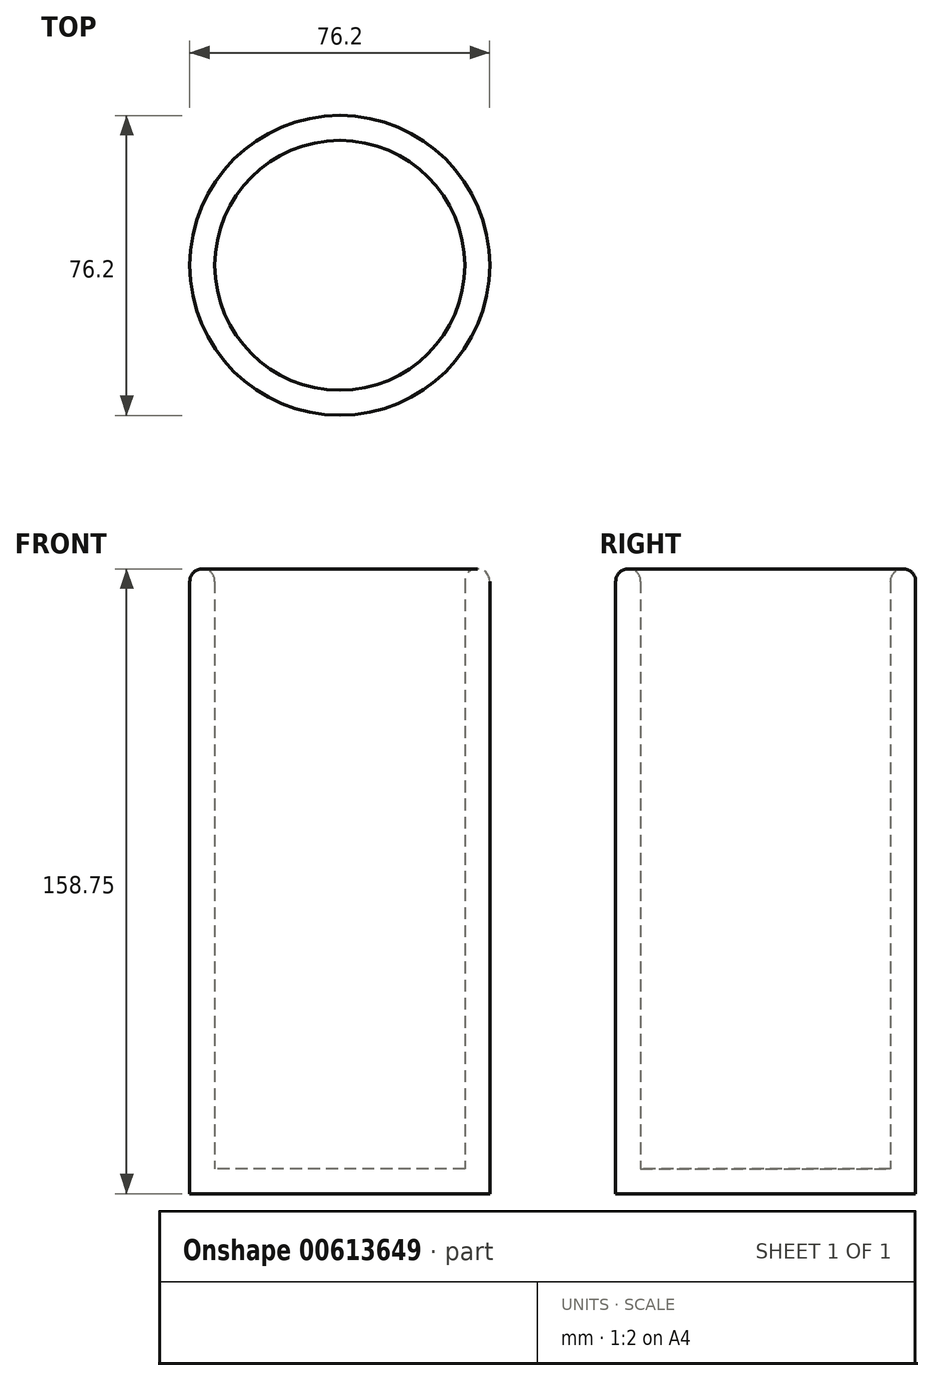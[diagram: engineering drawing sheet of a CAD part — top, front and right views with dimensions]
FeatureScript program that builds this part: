
annotation { "Feature Type Name" : "Feature", "Feature Type Description" : "" }
export const myFeature = defineFeature(function(context is Context, id is Id, definition is map)
    precondition{}
    {
        {
            var Q0;
            Q0=qCreatedBy(makeId("Top.planeOp"),FACE);
            var sketch = newSketch(context, id + "F0", { "sketchPlane" : qUnion([Q0])});
            skCircle(sketch, "E0", {"center": v(-62.36, 26.82) * mm, "radius": 38.1 * mm});
            skSolve(sketch);
        }
        {
            var Q0;
            Q0=makeQuery(id+"F0.imprint","IMPRINT",FACE,{"disambiguationData":[TD([[makeQuery(id+"F0.imprint","IMPRINT",EDGE,{"derivedFrom":sQuery(id+"F0.wireOp",EDGE,"E0")}),1.0]])]});
            extrude(context, id + "F1", {"entities" : qUnion([Q0]), "depth" : 6.35 * mm, "offsetDistance" : 25.4 * mm});
        }
        {
            var Q0;
            Q0=makeQuery(id+"F1.opExtrude","CAP_FACE",FACE,{"disambiguationData":[OSD([sQuery(id+"F0.wireOp",EDGE,"E0")])],"isStart":false});
            var sketch = newSketch(context, id + "F2", { "sketchPlane" : qUnion([Q0])});
            skCircle(sketch, "E1", {"center": v(-62.36, 26.82) * mm, "radius": 31.75 * mm});
            skSolve(sketch);
        }
        {
            var Q0;
            Q0=makeQuery(id+"F2.imprint","IMPRINT",FACE,{"disambiguationData":[TD([[makeQuery(id+"F2.imprint","IMPRINT",EDGE,{"derivedFrom":sQuery(id+"F2.wireOp",EDGE,"E1")}),-1.0]])]});
            extrude(context, id + "F3", {"entities" : qUnion([Q0]), "operationType" : NewBodyOperationType.ADD, "depth" : 152.4 * mm, "offsetDistance" : 25.4 * mm});
        }
        {
            var Q0;
            Q0=makeQuery(id+"F3.opExtrude","CAP_EDGE",EDGE,{"disambiguationData":[OSD([sQuery(id+"F2.wireOp",EDGE,"E1")])],"isStart":false});
            var Q1;
            Q1=makeQuery(id+"F3.opExtrude","CAP_EDGE",EDGE,{"disambiguationData":[OSD([sQuery(id+"F0.wireOp",EDGE,"E0")])],"isStart":false});
            fillet(context, id + "F4", {"entities" : qUnion([Q0, Q1]), "radius" : 3.17 * mm, "tangentPropagation" : true, "allowEdgeOverflow" : false});
        }
    });
